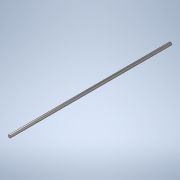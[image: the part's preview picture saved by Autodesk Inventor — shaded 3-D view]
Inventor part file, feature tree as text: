
AUTODESK INVENTOR PART (.ipt)
format: ipt  version: 2020 (Build 240168000, 168)  size: 109,568 bytes
history: native  units: in
note: dims shown in document units (in); Inventor stores cm internally (conversion verified against a paired STEP export)
features: extrude x1, sketch x1
ambient origin geometry x8: Origin, YZ Plane, XZ Plane, XY Plane, X Axis, Y Axis, Z Axis, Center Point
bodies: Solid1 (feature_tree)
feature tree (2):
  extrude  "Extrusion1"  Depth=33.0in TaperAngle=0.0deg
  sketch  "Sketch1"  dims[d0=0.5in d1=33.0in d2=0.0in]
